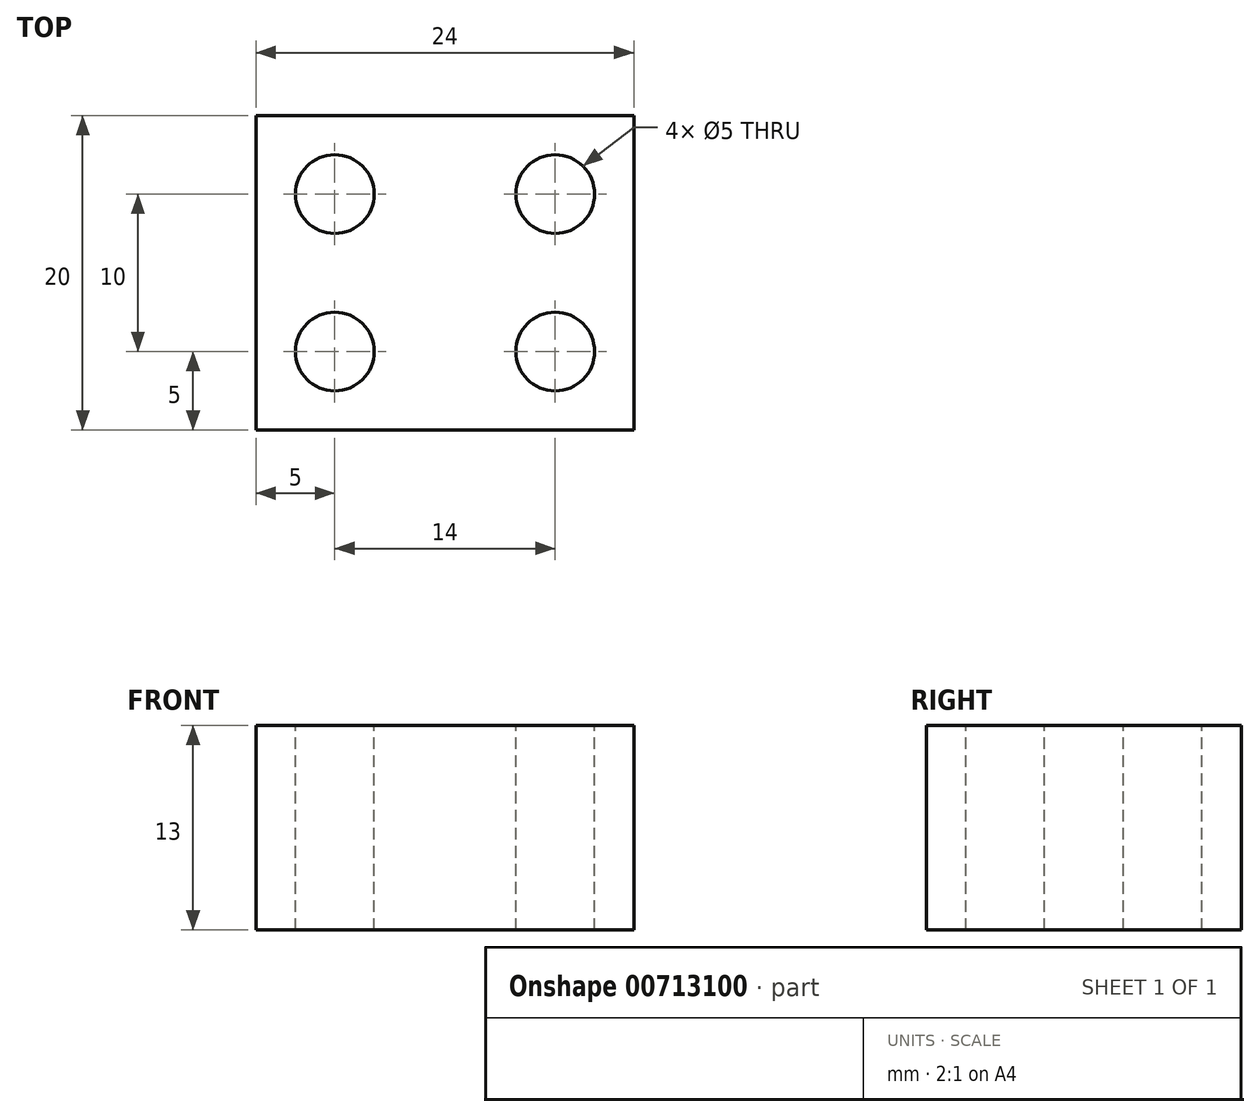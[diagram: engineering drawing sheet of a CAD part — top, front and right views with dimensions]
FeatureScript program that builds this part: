
annotation { "Feature Type Name" : "Feature", "Feature Type Description" : "" }
export const myFeature = defineFeature(function(context is Context, id is Id, definition is map)
    precondition{}
    {
        {
            var Q0;
            Q0=qCreatedBy(makeId("Top.planeOp"),FACE);
            var sketch = newSketch(context, id + "F0", { "sketchPlane" : qUnion([Q0])});
            skLineSegment(sketch, "E0.bottom", {"start": v(25.4, -25.4) * mm, "end": v(-25.4, -25.4) * mm});
            skLineSegment(sketch, "E0.top", {"start": v(25.4, 25.4) * mm, "end": v(-25.4, 25.4) * mm});
            skLineSegment(sketch, "E0.left", {"start": v(25.4, -25.4) * mm, "end": v(25.4, 25.4) * mm});
            skLineSegment(sketch, "E0.right", {"start": v(-25.4, -25.4) * mm, "end": v(-25.4, 25.4) * mm});
            skPoint(sketch, "E0.middle", {"position": v(0, 0) * mm});
            skSolve(sketch);
        }
        {
            var Q0;
            Q0=makeQuery(id+"F0.imprint","IMPRINT",FACE,{"disambiguationData":[TD([[makeQuery(id+"F0.imprint","IMPRINT",EDGE,{"derivedFrom":sQuery(id+"F0.wireOp",EDGE,"E0.bottom")}),-1.0]])]});
            extrude(context, id + "F1", {"entities" : qUnion([Q0]), "depth" : 13 * mm, "offsetDistance" : 25 * mm});
        }
        {
            var Q0;
            Q0=makeQuery(id+"F1.opExtrude","CAP_FACE",FACE,{"disambiguationData":[OSD([sQuery(id+"F0.wireOp",EDGE,"E0.bottom"),sQuery(id+"F0.wireOp",EDGE,"E0.top"),sQuery(id+"F0.wireOp",EDGE,"E0.left"),sQuery(id+"F0.wireOp",EDGE,"E0.right")])],"isStart":false});
            var sketch = newSketch(context, id + "F2", { "sketchPlane" : qUnion([Q0])});
            skLineSegment(sketch, "E1.bottom", {"start": v(-25.4, -25.4) * mm, "end": v(-1.4, -25.4) * mm});
            skLineSegment(sketch, "E1.top", {"start": v(-25.4, -5.4) * mm, "end": v(-1.4, -5.4) * mm});
            skLineSegment(sketch, "E1.left", {"start": v(-25.4, -25.4) * mm, "end": v(-25.4, -5.4) * mm});
            skLineSegment(sketch, "E1.right", {"start": v(-1.4, -25.4) * mm, "end": v(-1.4, -5.4) * mm});
            skSolve(sketch);
        }
        {
            var Q0;
            {var subQ4=sQuery(id+"F2.wireOp",EDGE,"E1.top");Q0=makeQuery(id+"F2.imprint","IMPRINT",FACE,{"disambiguationData":[TD([[makeQuery(id+"F2.imprint","IMPRINT",EDGE,{"derivedFrom":subQ4}),1.0]])]});}
            extrude(context, id + "F3", {"entities" : qUnion([Q0]), "operationType" : NewBodyOperationType.REMOVE, "oppositeDirection" : true, "depth" : 16 * mm, "offsetDistance" : 25 * mm});
        }
        {
            var Q0;
            Q0=makeQuery(id+"F1.opExtrude","CAP_FACE",FACE,{"disambiguationData":[OSD([sQuery(id+"F0.wireOp",EDGE,"E0.bottom"),sQuery(id+"F0.wireOp",EDGE,"E0.top"),sQuery(id+"F0.wireOp",EDGE,"E0.left"),sQuery(id+"F0.wireOp",EDGE,"E0.right")])],"isStart":false});
            var sketch = newSketch(context, id + "F4", { "sketchPlane" : qUnion([Q0])});
            skLineSegment(sketch, "E2.bottom", {"start": v(-6.4, -20.4) * mm, "end": v(-20.4, -20.4) * mm});
            skLineSegment(sketch, "E2.top", {"start": v(-6.4, -10.4) * mm, "end": v(-20.4, -10.4) * mm});
            skLineSegment(sketch, "E2.left", {"start": v(-6.4, -20.4) * mm, "end": v(-6.4, -10.4) * mm});
            skLineSegment(sketch, "E2.right", {"start": v(-20.4, -20.4) * mm, "end": v(-20.4, -10.4) * mm});
            skPoint(sketch, "E2.middle", {"position": v(-13.4, -15.4) * mm});
            skPoint(sketch, "E2.middle.positionSnap0", {"position": v(-13.4, -5.4) * mm});
            skPoint(sketch, "E2.middle.positionSnap1", {"position": v(-1.4, -15.4) * mm});
            skPoint(sketch, "E2.centerSnap0", {"position": v(-13.4, -5.4) * mm});
            skPoint(sketch, "E2.centerSnap1", {"position": v(-1.4, -15.4) * mm});
            skSolve(sketch);
        }
        {
            var Q0;
            Q0=sQuery(id+"F4.wireOp",VERTEX,"E2.top.end");
            var Q1;
            Q1=sQuery(id+"F4.wireOp",VERTEX,"E2.right.start");
            var Q2;
            Q2=sQuery(id+"F4.wireOp",VERTEX,"E2.left.end");
            var Q3;
            Q3=sQuery(id+"F4.wireOp",VERTEX,"E2.bottom.start");
            var Q4;
            Q4=makeQuery(id+"F1.opExtrude","SWEPT_BODY",BODY,{"disambiguationData":[OSD([sQuery(id+"F0.wireOp",EDGE,"E0.bottom"),sQuery(id+"F0.wireOp",EDGE,"E0.top"),sQuery(id+"F0.wireOp",EDGE,"E0.left"),sQuery(id+"F0.wireOp",EDGE,"E0.right")])]});
            hole(context, id + "F5", {"style" : HoleStyle.SIMPLE, "endStyle" : HoleEndStyle.THROUGH, "holeDiameter" : 5 * mm, "majorDiameter" : 5 * mm, "isTappedThrough" : true, "tappedDepth" : 12 * mm, "tapClearance" : 3, "locations" : qUnion([Q0, Q1, Q2, Q3]), "scope" : qUnion([Q4])});
        }
    });
